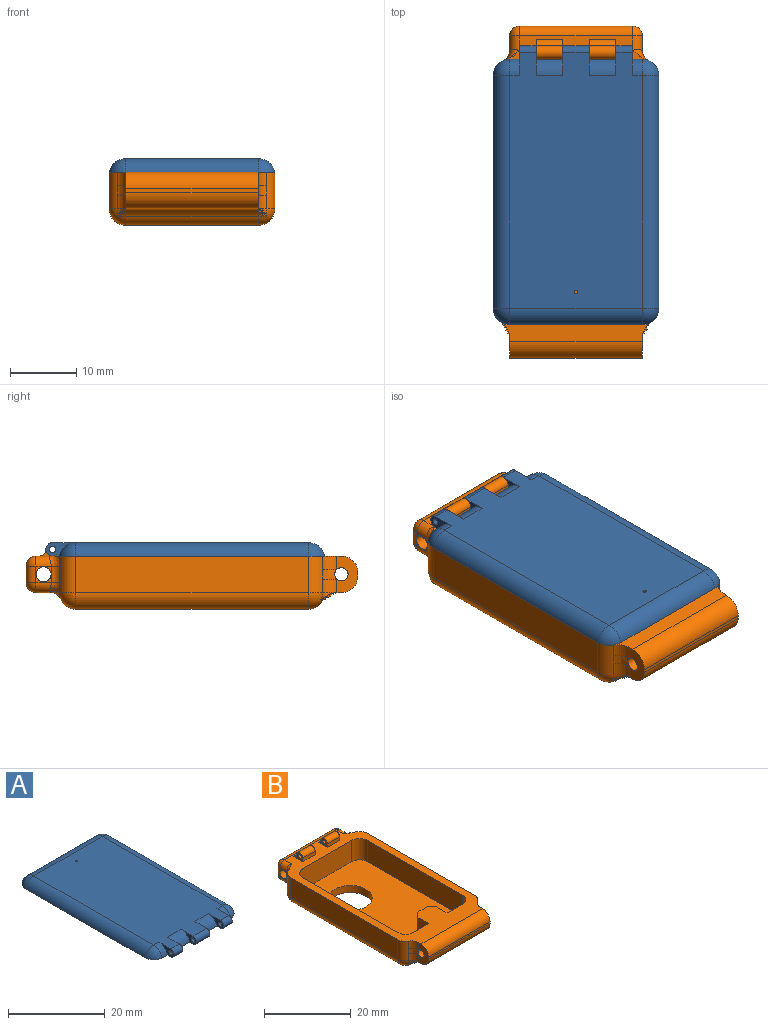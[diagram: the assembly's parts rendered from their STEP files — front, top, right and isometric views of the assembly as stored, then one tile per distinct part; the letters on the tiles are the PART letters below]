
ASSEMBLY  parts=2 mates=1
PART A: 26 faces, bbox 25x42x2 mm
  f0: plane 38.55x20.1mm, normal (0,0,1), area 736.4mm2, adj f2,f3,f4,f5,f6,f7,f11,f12
  f1: plane 41x25mm, normal (0,0,-1), area 1003.4mm2, adj f2,f3,f4,f5,f6,f7,f11,f12
  f2: plane 4.45x2mm, normal (-1,0,0), area 4mm2, adj f0,f1,f10,f11,f24
  f3: plane 4.45x2mm, normal (1,0,0), area 4mm2, adj f0,f1,f10,f21,f24
  f4: plane 4.45x2mm, normal (-1,0,0), area 4mm2, adj f0,f1,f9,f21,f23
  f5: plane 4.45x2mm, normal (1,0,0), area 4mm2, adj f0,f1,f9,f20,f23
  f6: plane 4.45x2mm, normal (-1,0,0), area 4mm2, adj f0,f1,f8,f20,f22
  f7: plane 4.45x2mm, normal (1,0,0), area 4mm2, adj f0,f1,f8,f19,f22
  f8: cylinder r=0.5mm len=2.5mm, axis (-1,0,0), area 7.9mm2, adj f6,f7
  f9: cylinder r=0.5mm len=4mm, axis (-1,0,0), area 12.6mm2, adj f4,f5
  f10: cylinder r=0.5mm len=2.5mm, axis (-1,0,0), area 7.9mm2, adj f2,f3
  f11: cylinder r=2.5mm len=2.45mm, axis (-1,0,0), area 5.1mm2, adj f0,f1,f2,f12
  f12: torus R=0.05mm, axis (0,0,-1), area 8.1mm2, adj f0,f1,f11,f13
  f13: cylinder r=2.5mm len=35mm, axis (0,1,0), area 119.8mm2, adj f0,f1,f12,f14
  f14: torus R=0.05mm, axis (0,0,-1), area 8.1mm2, adj f0,f1,f13,f15
  f15: cylinder r=2.5mm len=20mm, axis (-1,0,0), area 68.5mm2, adj f0,f1,f14,f16
  f16: torus R=0.05mm, axis (0,0,-1), area 8.1mm2, adj f0,f1,f15,f17
  f17: cylinder r=2.5mm len=35mm, axis (0,1,0), area 119.8mm2, adj f0,f1,f16,f18
  f18: torus R=0.05mm, axis (0,0,-1), area 8.1mm2, adj f0,f1,f17,f19
  f19: cylinder r=2.5mm len=2.45mm, axis (-1,0,0), area 5.1mm2, adj f0,f1,f7,f18
  f20: cylinder r=2.5mm len=4mm, axis (-1,0,0), area 13.7mm2, adj f0,f1,f5,f6
  f21: cylinder r=2.5mm len=4mm, axis (-1,0,0), area 13.7mm2, adj f0,f1,f3,f4
  f22: cylinder r=1mm len=2.5mm, axis (-1,0,0), area 7.9mm2, adj f0,f1,f6,f7
  f23: cylinder r=1mm len=4mm, axis (-1,0,0), area 12.6mm2, adj f0,f1,f4,f5
  f24: cylinder r=1mm len=2.5mm, axis (-1,0,0), area 7.9mm2, adj f0,f1,f2,f3
  f25: cylinder r=0.25mm len=2mm, axis (0,0,1), area 3.1mm2, adj f0,f1
PART B: 90 faces, bbox 28.2x50.6x11.9 mm
  f0: plane 6x5mm, normal (0,1,0), area 30mm2, adj f1,f9,f10,f71
  f1: plane 46.56x25.56mm, normal (0,0,1), area 360.6mm2, adj f0,f2,f3,f5,f6,f7,f8,f10
  f2: plane 35x5.5mm, normal (1,0,0), area 192.5mm2, adj f1,f19,f23,f25
  f3: plane 35x5.5mm, normal (-1,0,0), area 192.5mm2, adj f1,f14,f16,f17
  f4: plane 35x20mm, normal (0,0,-1), area 621.5mm2, adj f17,f18,f22,f23,f26
  f5: plane 31x6mm, normal (-1,0,0), area 186mm2, adj f1,f9,f11,f13
  f6: plane 16x6mm, normal (0,-1,0), area 96mm2, adj f1,f9,f12,f13
  f7: plane 31x6mm, normal (1,0,0), area 186mm2, adj f1,f9,f10,f12
  f8: plane 6x5mm, normal (0,1,0), area 30mm2, adj f1,f9,f11,f72
  f9: plane 36x21mm, normal (0,0,1), area 644.3mm2, adj f0,f5,f6,f7,f8,f10,f11,f12
  f10: cylinder r=2.5mm len=6mm, axis (0,0,-1), area 23.6mm2, adj f0,f1,f7,f9
  f11: cylinder r=2.5mm len=6mm, axis (0,0,1), area 23.6mm2, adj f1,f5,f8,f9
  f12: cylinder r=2.5mm len=6mm, axis (0,0,1), area 23.6mm2, adj f1,f6,f7,f9
  f13: cylinder r=2.5mm len=6mm, axis (0,0,-1), area 23.6mm2, adj f1,f5,f6,f9
  f14: cylinder r=2.5mm len=5.5mm, axis (0,0,1), area 14.4mm2, adj f1,f3,f15,f87,f88,f89
  f15: sphere r=2.5mm, area 8mm2, adj f14,f17,f18,f85,f86
  f16: cylinder r=2.5mm len=5.5mm, axis (0,0,-1), area 16.7mm2, adj f1,f3,f20,f53,f55,f57
  f17: cylinder r=2.5mm len=35mm, axis (0,-1,0), area 137.4mm2, adj f3,f4,f15,f20
  f18: cylinder r=2.5mm len=20mm, axis (1,0,0), area 52.4mm2, adj f4,f15,f21,f84
  f19: cylinder r=2.5mm len=5.5mm, axis (0,0,-1), area 14.4mm2, adj f1,f2,f21,f79,f80,f81
  f20: sphere r=2.5mm, area 9.6mm2, adj f16,f17,f22,f56
  f21: sphere r=2.5mm, area 8mm2, adj f18,f19,f23,f82,f83
  f22: cylinder r=2.5mm len=20mm, axis (-1,0,0), area 59.7mm2, adj f4,f20,f24,f51,f52,f54
  f23: cylinder r=2.5mm len=35mm, axis (0,1,0), area 137.4mm2, adj f2,f4,f21,f24
  f24: sphere r=2.5mm, area 9.6mm2, adj f22,f23,f25,f50
  f25: cylinder r=2.5mm len=5.5mm, axis (0,0,1), area 16.7mm2, adj f1,f2,f24,f47,f48,f49
  f26: cylinder r=5mm len=10mm, axis (0,0,1), area 62.8mm2, adj f4,f9
  f27: plane 5.5x3.17mm, normal (-1,0,0), area 11.9mm2, adj f1,f28,f30,f76,f77,f78,f87,f89
  f28: plane 20x0.67mm, normal (0,0,-1), area 13.4mm2, adj f27,f29,f77,f84
  f29: plane 5.5x3.17mm, normal (1,0,0), area 11.9mm2, adj f1,f28,f30,f76,f77,f78,f79,f81
  f30: plane 20x0.5mm, normal (0,-1,0), area 10mm2, adj f27,f29,f77,f78
  f31: plane 2.5x2.29mm, normal (1,0,0), area 1.8mm2, adj f40,f44,f46,f48,f58
  f32: plane 17x2.29mm, normal (0,0,-1), area 39mm2, adj f35,f39,f40,f52
  f33: plane 2.5x2.29mm, normal (-1,0,0), area 1.8mm2, adj f35,f37,f38,f55,f58
  f34: plane 17x2.5mm, normal (0,1,0), area 42.5mm2, adj f38,f39,f43,f44
  f35: cylinder r=1.5mm len=2.29mm, axis (0,-1,0), area 5.2mm2, adj f32,f33,f36,f54,f56,f57
  f36: sphere r=1.5mm, area 4.8mm2, adj f35,f38,f39
  f37: cylinder r=1.5mm len=2.29mm, axis (0,1,0), area 5.4mm2, adj f1,f33,f41,f53
  f38: cylinder r=1.5mm len=2.5mm, axis (0,0,1), area 5.9mm2, adj f33,f34,f36,f41
  f39: cylinder r=1.5mm len=17mm, axis (-1,0,0), area 40.1mm2, adj f32,f34,f36,f42
  f40: cylinder r=1.5mm len=2.29mm, axis (0,-1,0), area 5.2mm2, adj f31,f32,f42,f49,f50,f51
  f41: sphere r=1.5mm, area 4.8mm2, adj f37,f38,f43
  f42: sphere r=1.5mm, area 2.3mm2, adj f39,f40,f44
  f43: cylinder r=1.5mm len=17mm, axis (1,0,0), area 40.1mm2, adj f1,f34,f41,f45
  f44: cylinder r=1.5mm len=2.5mm, axis (0,0,-1), area 5.9mm2, adj f31,f34,f42,f45
  f45: sphere r=1.5mm, area 2.3mm2, adj f43,f44,f46
  f46: cylinder r=1.5mm len=2.29mm, axis (0,1,0), area 5.4mm2, adj f1,f31,f45,f47
  f47: bspline ~3.63x2.53mm, area 3.9mm2, adj f1,f25,f46,f48
  f48: cylinder r=1.5mm len=2.5mm, axis (0,0,1), area 4.4mm2, adj f25,f31,f47,f49
  f49: bspline ~2.45x1.58mm, area 2mm2, adj f25,f40,f48,f50
  f50: bspline ~1.77x1.69mm, area 1.5mm2, adj f24,f40,f49,f51
  f51: bspline ~2.45x1.58mm, area 2mm2, adj f22,f40,f50,f52
  f52: cylinder r=1.5mm len=17mm, axis (-1,0,0), area 30.3mm2, adj f22,f32,f51,f54
  f53: bspline ~3.63x2.53mm, area 3.9mm2, adj f1,f16,f37,f55
  f54: bspline ~2.45x1.58mm, area 2mm2, adj f22,f35,f52,f56
  f55: cylinder r=1.5mm len=2.5mm, axis (0,0,-1), area 4.4mm2, adj f16,f33,f53,f57
  f56: bspline ~1.77x1.69mm, area 1.5mm2, adj f20,f35,f54,f57
  f57: bspline ~2.45x1.58mm, area 2mm2, adj f16,f35,f55,f56
  f58: cylinder r=1.12mm len=20mm, axis (-1,0,0), area 141.4mm2, adj f31,f33
  f59: plane 3x2mm, normal (-1,0,0), area 3mm2, adj f1,f60,f66,f67,f68
  f60: plane 4x1mm, normal (0,-1,0), area 4mm2, adj f1,f59,f61,f67
  f61: plane 3x2mm, normal (1,0,0), area 3mm2, adj f1,f60,f66,f67,f68
  f62: plane 3x2mm, normal (-1,0,0), area 3mm2, adj f1,f63,f65,f69,f70
  f63: plane 4x1mm, normal (0,-1,0), area 4mm2, adj f1,f62,f64,f69
  f64: plane 3x2mm, normal (1,0,0), area 3mm2, adj f1,f63,f65,f69,f70
  f65: cylinder r=0.5mm len=4mm, axis (1,0,0), area 12.6mm2, adj f62,f64
  f66: cylinder r=0.5mm len=4mm, axis (1,0,0), area 12.6mm2, adj f59,f61
  f67: cylinder r=1mm len=4mm, axis (1,0,0), area 12.6mm2, adj f59,f60,f61,f68
  f68: cylinder r=1mm len=4mm, axis (-1,0,0), area 6.3mm2, adj f1,f59,f61,f67
  f69: cylinder r=1mm len=4mm, axis (1,0,0), area 12.6mm2, adj f62,f63,f64,f70
  f70: cylinder r=1mm len=4mm, axis (-1,0,0), area 6.3mm2, adj f1,f62,f64,f69
  f71: plane 6x3.5mm, normal (-1,0,0), area 21mm2, adj f0,f1,f9,f75
  f72: plane 6x3.5mm, normal (1,0,0), area 21mm2, adj f1,f8,f9,f74
  f73: plane 6x3mm, normal (0,1,0), area 18mm2, adj f1,f9,f74,f75
  f74: plane 6x1.5mm, normal (0.71,0.71,0), area 12.7mm2, adj f1,f9,f72,f73
  f75: plane 6x1.5mm, normal (-0.71,0.71,0), area 12.7mm2, adj f1,f9,f71,f73
  f76: cylinder r=1mm len=20mm, axis (1,0,0), area 125.7mm2, adj f27,f29,f80,f88
  f77: cylinder r=2.5mm len=20mm, axis (-1,0,0), area 78.5mm2, adj f27,f28,f29,f30
  f78: cylinder r=2.5mm len=20mm, axis (-1,0,0), area 78.5mm2, adj f1,f27,f29,f30
  f79: cylinder r=2.5mm len=2.17mm, axis (0,0,-1), area 5.3mm2, adj f1,f19,f29,f80
  f80: bspline ~2.17x1.49mm, area 3.5mm2, adj f19,f76,f79,f81
  f81: cylinder r=2.5mm len=2.17mm, axis (0,0,-1), area 5.3mm2, adj f19,f29,f80,f82
  f82: torus R=4.33mm, axis (-1,0,0), area 2.2mm2, adj f21,f81,f83
  f83: torus R=4.33mm, axis (0,0,1), area 2.2mm2, adj f21,f82,f84
  f84: cylinder r=2.5mm len=20mm, axis (1,0,0), area 52.4mm2, adj f18,f28,f83,f85
  f85: torus R=4.33mm, axis (0,0,1), area 2.2mm2, adj f15,f84,f86
  f86: torus R=4.33mm, axis (1,0,0), area 2.2mm2, adj f15,f85,f87
  f87: cylinder r=2.5mm len=2.17mm, axis (0,0,1), area 5.3mm2, adj f14,f27,f86,f88
  f88: bspline ~2.17x1.49mm, area 3.5mm2, adj f14,f76,f87,f89
  f89: cylinder r=2.5mm len=2.17mm, axis (0,0,1), area 5.3mm2, adj f1,f14,f27,f88
PLACE A rot(axis=(0,0,-1),180deg) t=(-1.93,-19.47,-0.78)mm
PLACE B t=(23.07,-19.47,-8.78)mm
MATE revolute A.f8 <-> B.f65  axis (1,0,0) through (4.57,-18.47,0.22)mm
